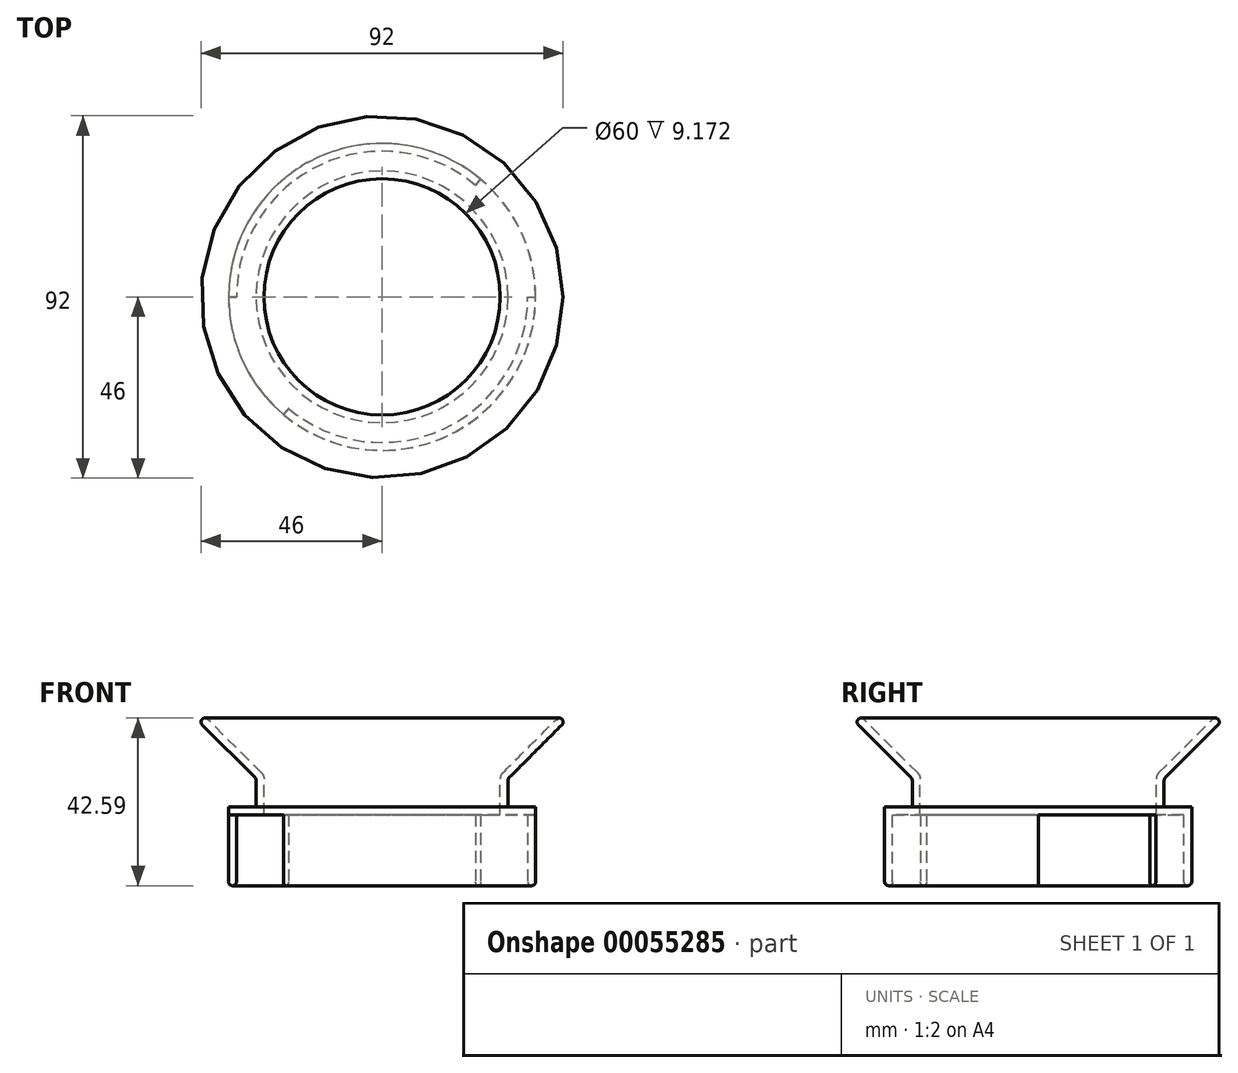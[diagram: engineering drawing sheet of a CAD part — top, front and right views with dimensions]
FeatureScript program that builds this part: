
annotation { "Feature Type Name" : "Feature", "Feature Type Description" : "" }
export const myFeature = defineFeature(function(context is Context, id is Id, definition is map)
    precondition{}
    {
        {
            var Q0;
            Q0=qCreatedBy(makeId("Front.planeOp"),FACE);
            var sketch = newSketch(context, id + "F0", { "sketchPlane" : qUnion([Q0])});
            skLineSegment(sketch, "E0", {"start": v(0, 0) * mm, "end": v(-39, 0) * mm});
            skLineSegment(sketch, "E1", {"start": v(-39, 0) * mm, "end": v(-39, 0) * mm});
            skLineSegment(sketch, "E2", {"start": v(-30, 29.78) * mm, "end": v(0, 29.78) * mm});
            skLineSegment(sketch, "E3", {"start": v(-30, 0) * mm, "end": v(-30, 9.17) * mm});
            skLineSegment(sketch, "E4", {"start": v(-44.3, 24.3) * mm, "end": v(-30.59, 10.59) * mm});
            skLineSegment(sketch, "E5", {"start": v(-45.7, 24.3) * mm, "end": v(-45.7, 24.3) * mm});
            skLineSegment(sketch, "E6", {"start": v(-30, 25) * mm, "end": v(-30, 10) * mm});
            skPoint(sketch, "E7.visualSharp", {"position": v(-39, 2) * mm});
            skPoint(sketch, "E8.visualSharp", {"position": v(-30, 10) * mm});
            skArc(sketch, "E8.filletArc", {"start": v(-30, 9.17) * mm, "mid": v(-30.15, 9.94) * mm, "end": v(-30.59, 10.59) * mm});
            skPoint(sketch, "E9.visualSharp", {"position": v(-46.41, 23.59) * mm});
            skArc(sketch, "E9.filletArc", {"start": v(-45.7, 24.3) * mm, "mid": v(-46, 23.59) * mm, "end": v(-45.7, 22.88) * mm});
            skPoint(sketch, "E10.visualSharp", {"position": v(-45, 25) * mm});
            skArc(sketch, "E10.filletArc", {"start": v(-44.3, 24.3) * mm, "mid": v(-45, 24.59) * mm, "end": v(-45.7, 24.3) * mm});
            skPoint(sketch, "E11.visualSharp", {"position": v(-32, 2) * mm});
            skLineSegment(sketch, "E12", {"start": v(-39, 2) * mm, "end": v(-39, 0) * mm});
            skLineSegment(sketch, "E13", {"start": v(-39, 2) * mm, "end": v(-32, 2) * mm});
            skLineSegment(sketch, "E14", {"start": v(-32, 2) * mm, "end": v(-32, 8.76) * mm});
            skLineSegment(sketch, "E15", {"start": v(-45.7, 22.88) * mm, "end": v(-32.3, 9.46) * mm});
            skArc(sketch, "E16.filletArc", {"start": v(-32, 8.76) * mm, "mid": v(-32.08, 9.14) * mm, "end": v(-32.3, 9.46) * mm});
            skSolve(sketch);
        }
        {
            var Q0;
            Q0=qCreatedBy(makeId("Front.planeOp"),FACE);
            var sketch = newSketch(context, id + "F1", { "sketchPlane" : qUnion([Q0])});
            skLineSegment(sketch, "E17", {"start": v(-37, 0) * mm, "end": v(-39, 0) * mm});
            skLineSegment(sketch, "E18", {"start": v(37, 0) * mm, "end": v(39, 0) * mm});
            skPoint(sketch, "E18.endSnap0", {"position": v(-38, 0) * mm});
            skLineSegment(sketch, "E19", {"start": v(-38, -18) * mm, "end": v(-38, -18) * mm});
            skLineSegment(sketch, "E20", {"start": v(38, -18) * mm, "end": v(38, -18) * mm});
            skLineSegment(sketch, "E21", {"start": v(37, 0) * mm, "end": v(37, -17) * mm});
            skLineSegment(sketch, "E22", {"start": v(39, 0) * mm, "end": v(39, -17) * mm});
            skLineSegment(sketch, "E23", {"start": v(-39, 0) * mm, "end": v(-39, -17) * mm});
            skLineSegment(sketch, "E24", {"start": v(-37, 0) * mm, "end": v(-37, -17) * mm});
            skPoint(sketch, "E25.visualSharp", {"position": v(-39, -18) * mm});
            skArc(sketch, "E25.filletArc", {"start": v(-39, -17) * mm, "mid": v(-38.7, -17.7) * mm, "end": v(-38, -18) * mm});
            skPoint(sketch, "E26.visualSharp", {"position": v(-37, -18) * mm});
            skArc(sketch, "E26.filletArc", {"start": v(-38, -18) * mm, "mid": v(-37.3, -17.7) * mm, "end": v(-37, -17) * mm});
            skPoint(sketch, "E27.visualSharp", {"position": v(37, -18) * mm});
            skArc(sketch, "E27.filletArc", {"start": v(37, -17) * mm, "mid": v(37.3, -17.7) * mm, "end": v(38, -18) * mm});
            skPoint(sketch, "E28.visualSharp", {"position": v(39, -18) * mm});
            skArc(sketch, "E28.filletArc", {"start": v(38, -18) * mm, "mid": v(38.7, -17.7) * mm, "end": v(39, -17) * mm});
            skSolve(sketch);
        }
        {
            var Q0;
            Q0=qCreatedBy(makeId("Front.planeOp"),FACE);
            var sketch = newSketch(context, id + "F2", { "sketchPlane" : qUnion([Q0])});
            skLineSegment(sketch, "E29", {"start": v(0, 33.15) * mm, "end": v(0, -29.85) * mm});
            skSolve(sketch);
        }
        {
            var Q0;
            Q0 = qSketchRegion(id + "F0", true);
            var Q1;
            Q1=sQuery(id+"F2.wireOp",EDGE,"E29");
            revolve(context, id + "F3", {"entities" : qUnion([Q0]), "axis" : qUnion([Q1]), "revolveType" : RevolveType.FULL});
        }
        {
            var Q0;
            Q0=qCreatedBy(makeId("Front.planeOp"),FACE);
            var sketch = newSketch(context, id + "F4", { "sketchPlane" : qUnion([Q0])});
            skLineSegment(sketch, "E30", {"start": v(0, 41.51) * mm, "end": v(0, -36.9) * mm});
            skSolve(sketch);
        }
        {
            var Q0;
            Q0 = qSketchRegion(id + "F1", true);
            var Q1;
            Q1=sQuery(id+"F4.wireOp",EDGE,"E30");
            revolve(context, id + "F5", {"operationType" : NewBodyOperationType.ADD, "entities" : qUnion([Q0]), "axis" : qUnion([Q1]), "revolveType" : RevolveType.ONE_DIRECTION, "angle" : 130 * degree});
        }
    });
